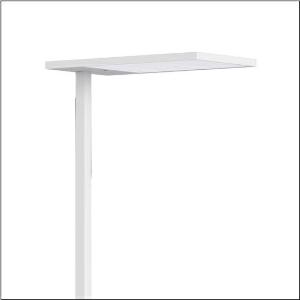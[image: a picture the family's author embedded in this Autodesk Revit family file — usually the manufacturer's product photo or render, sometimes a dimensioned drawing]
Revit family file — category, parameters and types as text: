
# Revit family: silica_r__21_floor_r_51mx53sg4dw_45fa
name_source: partatom
category: Lighting Fixtures
units: mm (PartAtom-declared; Revit-internal decimal feet)

## family parameters
Cut with Voids When Loaded = No
Host = Face
Light Source = No
Part Type = Normal
Room Calculation Point = No
Round Connector Dimension = Use Diameter
Shared = No

## types (1)
- Silica® 21 Floor R (1 x LED, 15000 lm, 106.4 W, 4000K)
    Apparent Load = 106 VA
    CIE Flux Codes = 54 86 97 13 100
    Color Rendering = 80
    Color Temperature = 4000K
    Default Elevation = 1800 mm
    Description = Silica® 21 Floor R, floorstanding luminaire, of PMMA, primary optical cover: prismatic diffuser, of PMMA, CAT 2 (L<= 3000cd/m²), light emission: indirect/direct distribution, primary light characteristic: symmetric, installation type: not mounted, LED, rated luminous flux: 15.000lm, luminous efficacy: 141lm/W, light colour: 840, colour temperature: 4000K, control gear: ECG DALI, daylight-dependent control, mains connection: 230V, 50Hz, connection cable pre-assembled, cable length: 2,5m, rated input power: 106.4W, luminaire head, of aluminium, traffic white (RAL 9016), length: 650mm, width: 350mm, supporting column, angular, of aluminium, traffic white (RAL 9016), baseplate, of steel, traffic white (RAL 9016), protection rating (complete): IP20, insulation class (complete): insulation class I (protective earthing), certification: CE, standard: EN 50419, packaging unit: 1 piece
    Height = 18 mm
    Lamp = 1 x LED
    Lamp Light Flux = 15000 lm
    Lamp Power = 106.4 W
    Lamp count = 1
    Length = 650 mm
    Luminous efficacy = 141 lm/W
    Manufacturer = Siteco
    ModVariant = No
    Model = 51MX53SG4DW
    Mounting Place = Floor
    Mounting Type = Freestanding
    Number of Poles = 1
    OnlyDefault = Yes
    Power Factor = 1
    Product Name = Silica® 21 Floor R
    Product group = floorstanding luminaire
    ProductGroupID = 1301
    Protection Class = Protection class I
    Protection Degree = IP 20
    RLX_Detail_Level = 1
    RLX_Emergency_Light_Flux = 0 lm
    RLX_Emergency_Type = 0
    RLX_Emergency_Type_DB = No
    RlxData = <blob elided: 18621 chars, md5=027db54a>
    Socket = socket
    Standby Power = 0 W
    System Light Flux = 15000 lm
    System Power = 106 W
    Type Comments = Product without accessories
    Type Image = l_1003935.jpg
    URL = http://relux.com
    VarID = ---
    Voltage = 0 V
    Weight = 0.00 kg
    Width = 350 mm

## geometry (parser evidence)
native form markers: Blend x4, Sweep x16
no freeform markers — native parametric forms only
